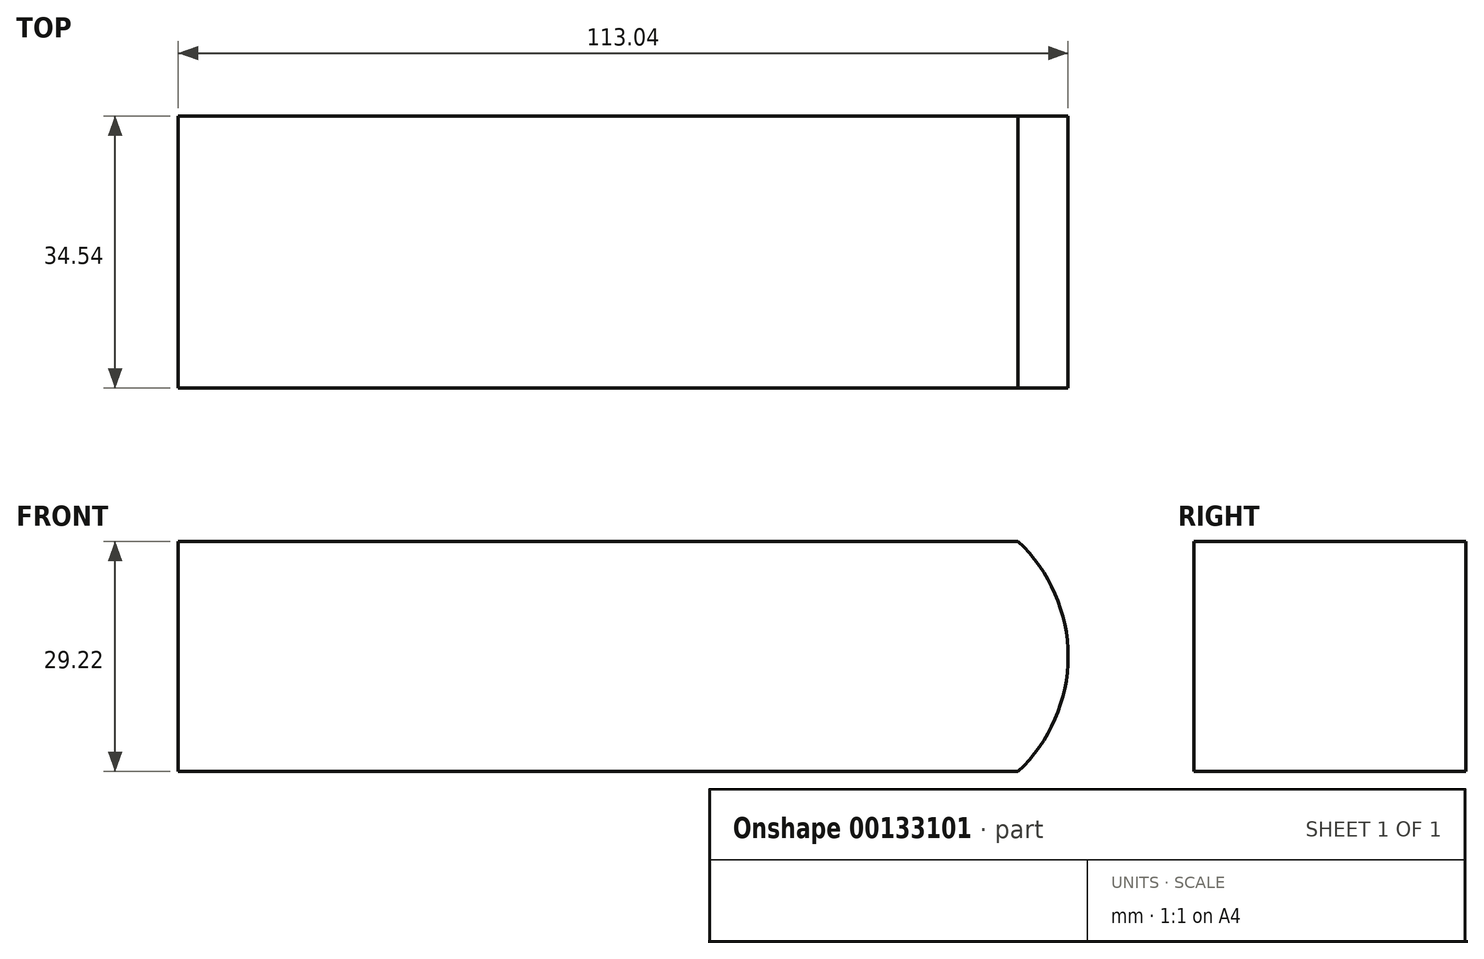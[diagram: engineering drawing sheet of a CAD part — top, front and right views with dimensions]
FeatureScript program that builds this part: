
annotation { "Feature Type Name" : "Feature", "Feature Type Description" : "" }
export const myFeature = defineFeature(function(context is Context, id is Id, definition is map)
    precondition{}
    {
        {
            var Q0;
            Q0=qCreatedBy(makeId("Top.planeOp"),FACE);
            var sketch = newSketch(context, id + "F0", { "sketchPlane" : qUnion([Q0])});
            skLineSegment(sketch, "E0.bottom", {"start": v(56.52, 17.27) * mm, "end": v(-56.52, 17.27) * mm});
            skLineSegment(sketch, "E0.top", {"start": v(56.52, -17.27) * mm, "end": v(-56.52, -17.27) * mm});
            skLineSegment(sketch, "E0.left", {"start": v(56.52, 17.27) * mm, "end": v(56.52, -17.27) * mm});
            skLineSegment(sketch, "E0.right", {"start": v(-56.52, 17.27) * mm, "end": v(-56.52, -17.27) * mm});
            skPoint(sketch, "E0.middle", {"position": v(0, 0) * mm});
            skSolve(sketch);
        }
        {
            var Q0;
            {var subQ4=sQuery(id+"F0.wireOp",EDGE,"E0.right");Q0=makeQuery(id+"F0.imprint","IMPRINT",FACE,{"disambiguationData":[TD([[makeQuery(id+"F0.imprint","IMPRINT",EDGE,{"derivedFrom":subQ4}),1.0]])]});}
            extrude(context, id + "F1", {"entities" : qUnion([Q0]), "endBound" : BoundingType.SYMMETRIC, "depth" : 29.2 * mm});
        }
        {
            var Q0;
            Q0=makeQuery(id+"F1.opExtrude","SWEPT_FACE",FACE,{"disambiguationData":[OSD([sQuery(id+"F0.wireOp",EDGE,"E0.top")])]});
            var sketch = newSketch(context, id + "F2", { "sketchPlane" : qUnion([Q0])});
            skArc(sketch, "E1", {"start": v(50.17, -14.6) * mm, "mid": v(56.52, 0) * mm, "end": v(50.17, 14.6) * mm});
            skSolve(sketch);
        }
        {
            var Q0;
            {var subQ0=sQuery(id+"F2.wireOp",EDGE,"E1");var subQ1=sQuery(id+"F0.wireOp",EDGE,"E0.top");var subQ2=makeQuery(id+"F1.opExtrude","CAP_EDGE",EDGE,{"disambiguationData":[OSD([subQ1])],"isStart":false});var subQ3=makeQuery(id+"F2.imprint","INTERSECT",VERTEX,{"derivedFrom":[subQ2,subQ0]});Q0=makeQuery(id+"F2.imprint","IMPRINT",FACE,{"disambiguationData":[TD([[makeQuery(id+"F2.imprint","IMPRINT",EDGE,{"disambiguationData":[TD([[subQ3,1.0]])],"derivedFrom":subQ0}),-1.0]])]});}
            var Q1;
            {var subQ0=sQuery(id+"F2.wireOp",EDGE,"E1");var subQ1=sQuery(id+"F0.wireOp",EDGE,"E0.top");var subQ2=makeQuery(id+"F1.opExtrude","CAP_EDGE",EDGE,{"disambiguationData":[OSD([subQ1])],"isStart":true});var subQ3=makeQuery(id+"F2.imprint","INTERSECT",VERTEX,{"derivedFrom":[subQ2,subQ0]});Q1=makeQuery(id+"F2.imprint","IMPRINT",FACE,{"disambiguationData":[TD([[makeQuery(id+"F2.imprint","IMPRINT",EDGE,{"disambiguationData":[TD([[subQ3,-1.0]])],"derivedFrom":subQ0}),-1.0]])]});}
            extrude(context, id + "F3", {"entities" : qUnion([Q0, Q1]), "operationType" : NewBodyOperationType.REMOVE, "endBound" : BoundingType.THROUGH_ALL, "oppositeDirection" : true, "depth" : 25.4 * mm});
        }
    });
